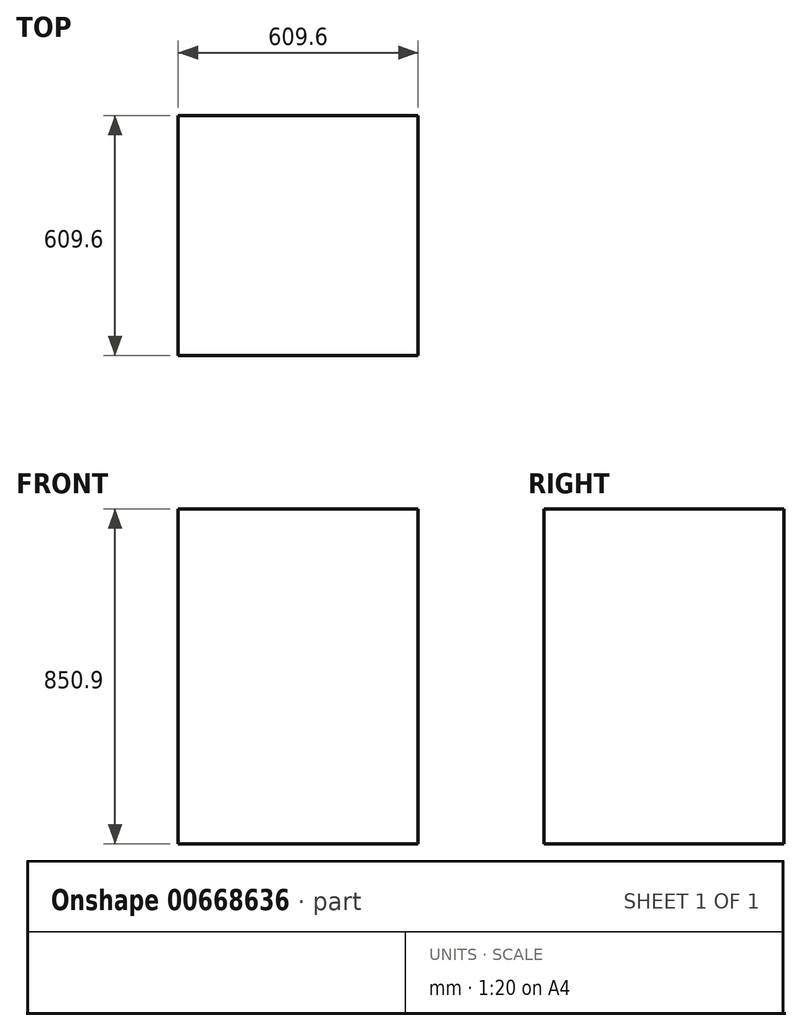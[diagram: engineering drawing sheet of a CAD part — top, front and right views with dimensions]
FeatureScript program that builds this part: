
annotation { "Feature Type Name" : "Feature", "Feature Type Description" : "" }
export const myFeature = defineFeature(function(context is Context, id is Id, definition is map)
    precondition{}
    {
        {
            var Q0;
            Q0=qCreatedBy(makeId("Front.planeOp"),FACE);
            var sketch = newSketch(context, id + "F0", { "sketchPlane" : qUnion([Q0])});
            skLineSegment(sketch, "E0.bottom", {"start": v(-304.8, 425.45) * mm, "end": v(304.8, 425.45) * mm});
            skLineSegment(sketch, "E0.top", {"start": v(-304.8, -425.45) * mm, "end": v(304.8, -425.45) * mm});
            skLineSegment(sketch, "E0.left", {"start": v(-304.8, 425.45) * mm, "end": v(-304.8, -425.45) * mm});
            skLineSegment(sketch, "E0.right", {"start": v(304.8, 425.45) * mm, "end": v(304.8, -425.45) * mm});
            skSolve(sketch);
        }
        {
            var Q0;
            Q0 = qSketchRegion(id + "F0", true);
            extrude(context, id + "F1", {"entities" : qUnion([Q0]), "depth" : 609.6 * mm, "offsetDistance" : 25.4 * mm, "symmetric" : true});
        }
    });
